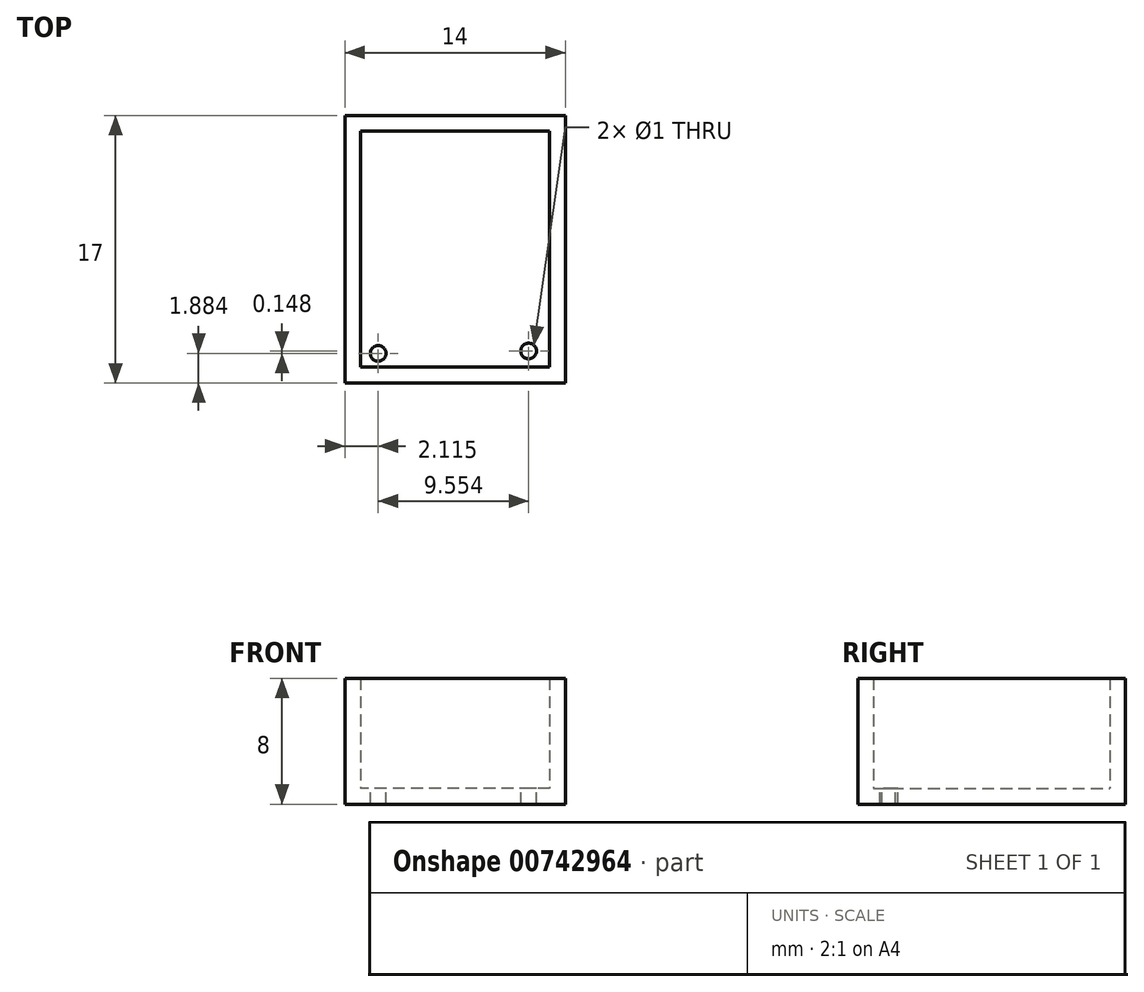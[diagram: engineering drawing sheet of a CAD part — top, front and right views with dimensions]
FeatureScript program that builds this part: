
annotation { "Feature Type Name" : "Feature", "Feature Type Description" : "" }
export const myFeature = defineFeature(function(context is Context, id is Id, definition is map)
    precondition{}
    {
        {
            var Q0;
            Q0=qCreatedBy(makeId("Top.planeOp"),FACE);
            var sketch = newSketch(context, id + "F0", { "sketchPlane" : qUnion([Q0])});
            skLineSegment(sketch, "E0.bottom", {"start": v(40.3, -33.77) * mm, "end": v(26.3, -33.77) * mm});
            skLineSegment(sketch, "E0.top", {"start": v(40.3, -16.77) * mm, "end": v(26.3, -16.77) * mm});
            skLineSegment(sketch, "E0.left", {"start": v(40.3, -33.77) * mm, "end": v(40.3, -16.77) * mm});
            skLineSegment(sketch, "E0.right", {"start": v(26.3, -33.77) * mm, "end": v(26.3, -16.77) * mm});
            skSolve(sketch);
        }
        {
            var Q0;
            Q0=makeQuery(id+"F0.imprint","IMPRINT",FACE,{"disambiguationData":[TD([[makeQuery(id+"F0.imprint","IMPRINT",EDGE,{"derivedFrom":sQuery(id+"F0.wireOp",EDGE,"E0.bottom")}),-1.0]])]});
            extrude(context, id + "F1", {"entities" : qUnion([Q0]), "depth" : 1 * mm, "offsetDistance" : 25 * mm});
        }
        {
            var Q0;
            Q0=makeQuery(id+"F1.opExtrude","CAP_FACE",FACE,{"disambiguationData":[OSD([sQuery(id+"F0.wireOp",EDGE,"E0.bottom"),sQuery(id+"F0.wireOp",EDGE,"E0.top"),sQuery(id+"F0.wireOp",EDGE,"E0.left"),sQuery(id+"F0.wireOp",EDGE,"E0.right")])],"isStart":false});
            var sketch = newSketch(context, id + "F2", { "sketchPlane" : qUnion([Q0])});
            skLineSegment(sketch, "E1.bottom", {"start": v(39.3, -32.77) * mm, "end": v(27.3, -32.77) * mm});
            skLineSegment(sketch, "E1.top", {"start": v(39.3, -17.77) * mm, "end": v(27.3, -17.77) * mm});
            skLineSegment(sketch, "E1.left", {"start": v(39.3, -32.77) * mm, "end": v(39.3, -17.77) * mm});
            skLineSegment(sketch, "E1.right", {"start": v(27.3, -32.77) * mm, "end": v(27.3, -17.77) * mm});
            skSolve(sketch);
        }
        {
            var Q0;
            Q0=makeQuery(id+"F2.imprint","IMPRINT",FACE,{"disambiguationData":[TD([[makeQuery(id+"F2.imprint","IMPRINT",EDGE,{"derivedFrom":sQuery(id+"F2.wireOp",EDGE,"E1.bottom")}),1.0]])]});
            extrude(context, id + "F3", {"entities" : qUnion([Q0]), "operationType" : NewBodyOperationType.ADD, "depth" : 7 * mm, "offsetDistance" : 25 * mm});
        }
        {
            var Q0;
            Q0=makeQuery(id+"F1.opExtrude","CAP_FACE",FACE,{"disambiguationData":[OSD([sQuery(id+"F0.wireOp",EDGE,"E0.bottom"),sQuery(id+"F0.wireOp",EDGE,"E0.top"),sQuery(id+"F0.wireOp",EDGE,"E0.left"),sQuery(id+"F0.wireOp",EDGE,"E0.right")])],"isStart":false});
            var sketch = newSketch(context, id + "F4", { "sketchPlane" : qUnion([Q0])});
            skCircle(sketch, "E2", {"center": v(37.96, -31.74) * mm, "radius": 0.5 * mm});
            skCircle(sketch, "E3", {"center": v(28.4, -31.89) * mm, "radius": 0.5 * mm});
            skSolve(sketch);
        }
        {
            var Q0;
            Q0=sQuery(id+"F4.wireOp",VERTEX,"E3.center");
            var Q1;
            Q1=sQuery(id+"F4.wireOp",VERTEX,"E2.center");
            var Q2;
            Q2=makeQuery(id+"F1.opExtrude","SWEPT_BODY",BODY,{"disambiguationData":[OSD([sQuery(id+"F0.wireOp",EDGE,"E0.bottom"),sQuery(id+"F0.wireOp",EDGE,"E0.top"),sQuery(id+"F0.wireOp",EDGE,"E0.left"),sQuery(id+"F0.wireOp",EDGE,"E0.right")])]});
            hole(context, id + "F5", {"style" : HoleStyle.SIMPLE, "endStyle" : HoleEndStyle.THROUGH, "holeDiameter" : 1 * mm, "majorDiameter" : 5 * mm, "isTappedThrough" : true, "tappedDepth" : 12 * mm, "tapClearance" : 3, "locations" : qUnion([Q0, Q1]), "scope" : qUnion([Q2])});
        }
    });
